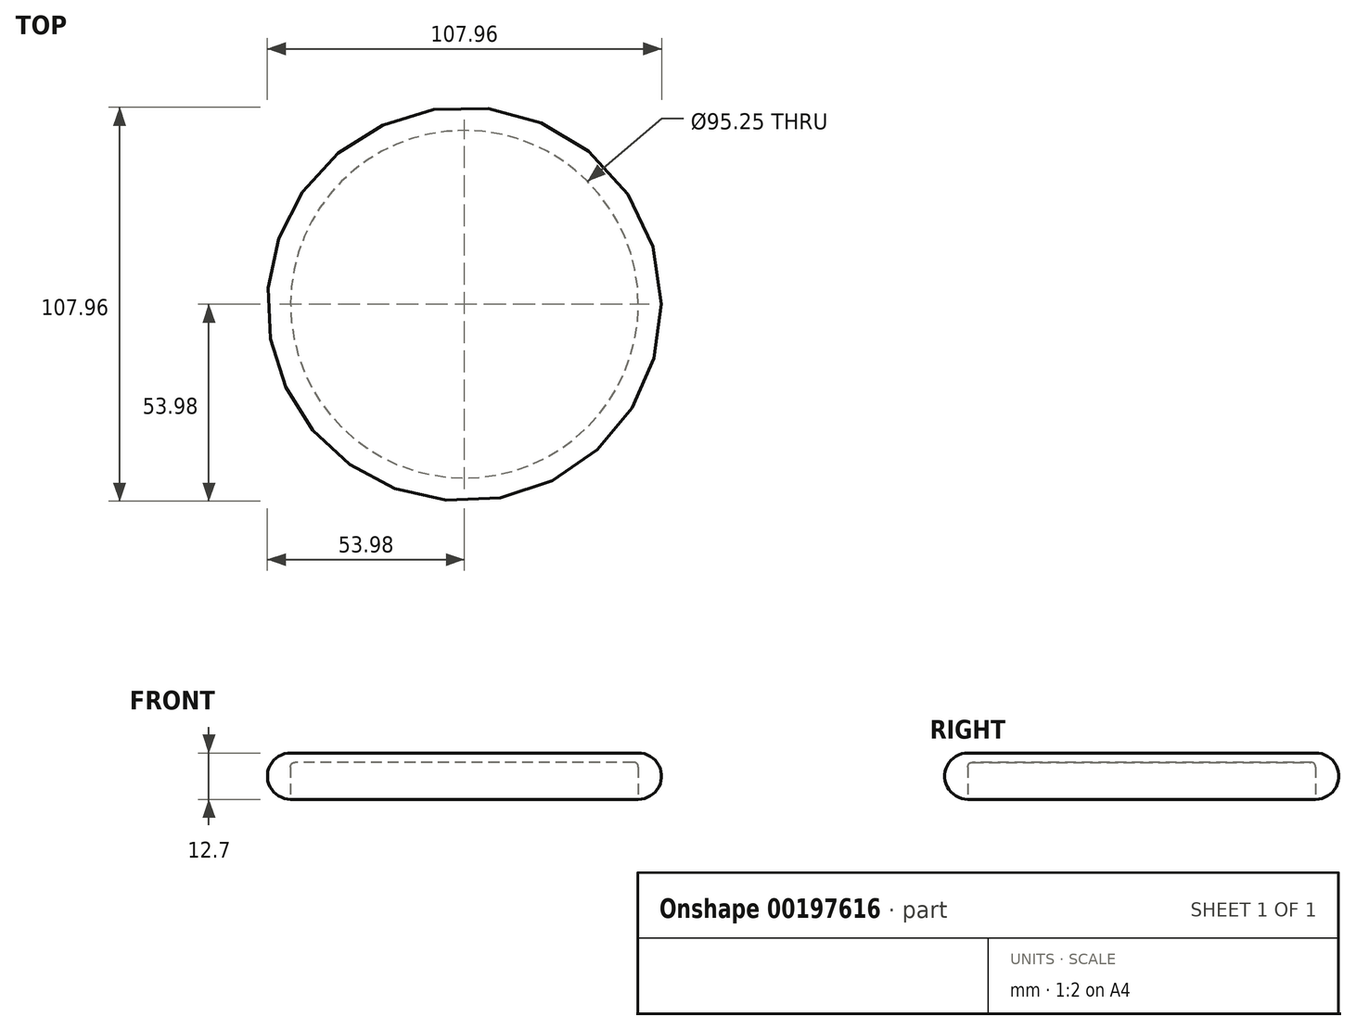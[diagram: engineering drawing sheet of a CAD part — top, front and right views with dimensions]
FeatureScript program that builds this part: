
annotation { "Feature Type Name" : "Feature", "Feature Type Description" : "" }
export const myFeature = defineFeature(function(context is Context, id is Id, definition is map)
    precondition{}
    {
        {
            var Q0;
            Q0=qCreatedBy(makeId("Top.planeOp"),FACE);
            var sketch = newSketch(context, id + "F0", { "sketchPlane" : qUnion([Q0])});
            skCircle(sketch, "E0", {"center": v(0, 0) * mm, "radius": 53.98 * mm});
            skSolve(sketch);
        }
        {
            var Q0;
            Q0 = qSketchRegion(id + "F0", true);
            extrude(context, id + "F1", {"entities" : qUnion([Q0]), "depth" : 12.7 * mm});
        }
        {
            var Q0;
            Q0=makeQuery(id+"F1.opExtrude","SWEPT_FACE",FACE,{"disambiguationData":[OSD([sQuery(id+"F0.wireOp",EDGE,"E0")])]});
            fillet(context, id + "F2", {"entities" : qUnion([Q0]), "radius" : 6.35 * mm, "allowEdgeOverflow" : false});
        }
        {
            var Q0;
            Q0=makeQuery(id+"F1.opExtrude","CAP_FACE",FACE,{"disambiguationData":[OSD([sQuery(id+"F0.wireOp",EDGE,"E0")])],"isStart":true});
            extrude(context, id + "F3", {"entities" : qUnion([Q0]), "operationType" : NewBodyOperationType.REMOVE, "oppositeDirection" : true, "depth" : 10.16 * mm});
        }
        {
            var Q0;
            Q0=makeQuery(id+"F3.boolean.opBoolean","COPY",EDGE,{"derivedFrom":makeQuery(id+"F3.opExtrude","CAP_EDGE",EDGE,{"disambiguationData":[OSD([sQuery(id+"F0.wireOp",EDGE,"E0")])],"isStart":false})});
            fillet(context, id + "F4", {"entities" : qUnion([Q0]), "radius" : 1.27 * mm, "tangentPropagation" : true, "allowEdgeOverflow" : false});
        }
    });
